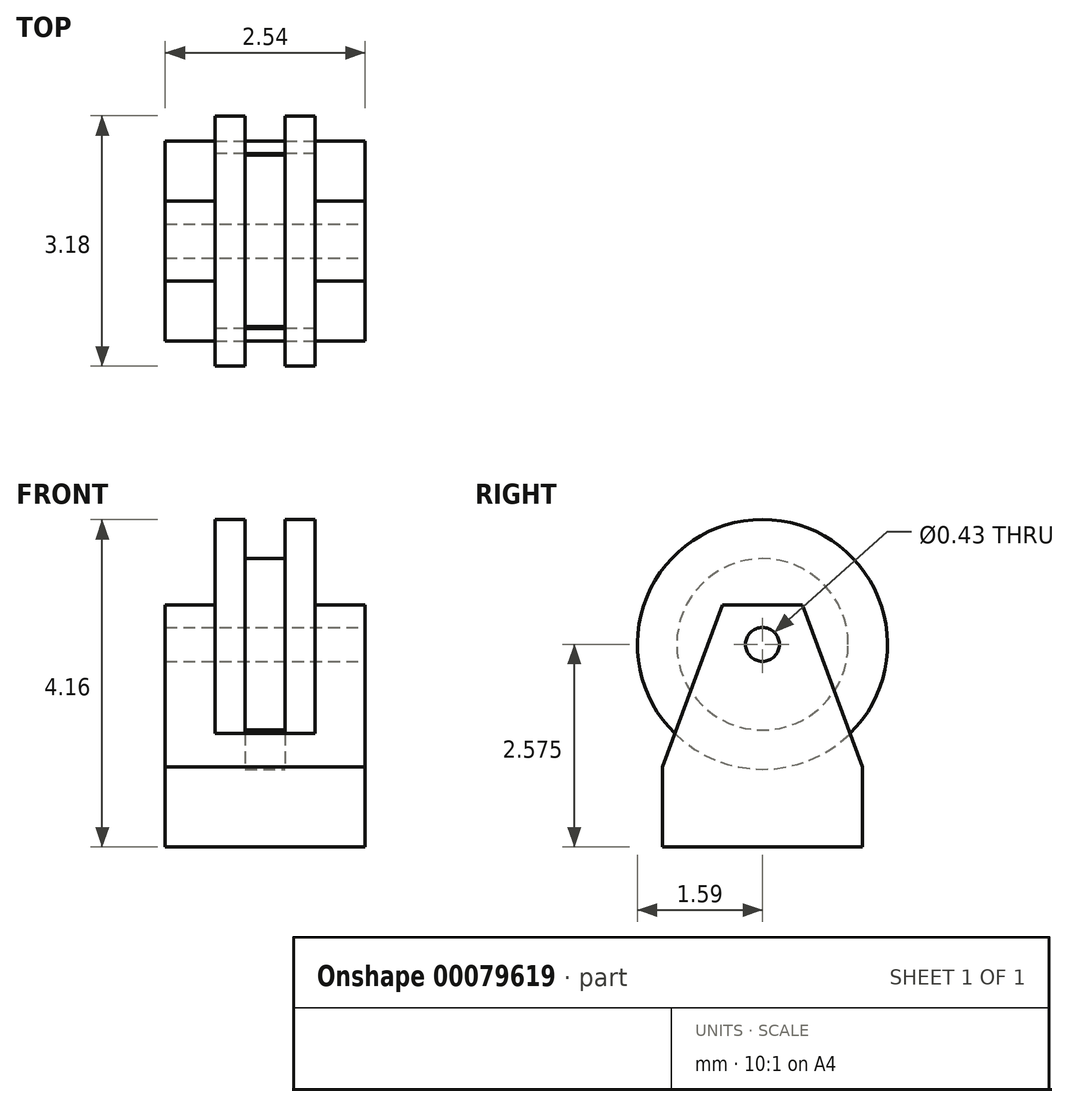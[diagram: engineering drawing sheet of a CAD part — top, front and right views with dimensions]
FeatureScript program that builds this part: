
annotation { "Feature Type Name" : "Feature", "Feature Type Description" : "" }
export const myFeature = defineFeature(function(context is Context, id is Id, definition is map)
    precondition{}
    {
        {
            var Q0;
            Q0=qCreatedBy(makeId("Top.planeOp"),FACE);
            var sketch = newSketch(context, id + "F0", { "sketchPlane" : qUnion([Q0])});
            skLineSegment(sketch, "E0.bottom", {"start": v(-1.27, 1.27) * mm, "end": v(1.27, 1.27) * mm});
            skLineSegment(sketch, "E0.top", {"start": v(-1.27, -1.27) * mm, "end": v(1.27, -1.27) * mm});
            skLineSegment(sketch, "E0.left", {"start": v(-1.27, 1.27) * mm, "end": v(-1.27, -1.27) * mm});
            skLineSegment(sketch, "E0.right", {"start": v(1.27, 1.27) * mm, "end": v(1.27, -1.27) * mm});
            skSolve(sketch);
        }
        {
            var Q0;
            Q0 = qSketchRegion(id + "F0", true);
            extrude(context, id + "F1", {"entities" : qUnion([Q0]), "depth" : 1.02 * mm});
        }
        {
            var Q0;
            Q0=qCreatedBy(makeId("Right.planeOp"),FACE);
            var sketch = newSketch(context, id + "F2", { "sketchPlane" : qUnion([Q0])});
            skCircle(sketch, "E1", {"center": v(0, 2.58) * mm, "radius": 1.59 * mm});
            skSolve(sketch);
        }
        {
            var Q0;
            Q0 = qSketchRegion(id + "F2", true);
            extrude(context, id + "F3", {"entities" : qUnion([Q0]), "operationType" : NewBodyOperationType.ADD, "depth" : 1.27 * mm, "symmetric" : true});
        }
        {
            var Q0;
            Q0=makeQuery(id+"F1.opExtrude","SWEPT_FACE",FACE,{"disambiguationData":[OSD([sQuery(id+"F0.wireOp",EDGE,"E0.right")])]});
            var sketch = newSketch(context, id + "F4", { "sketchPlane" : qUnion([Q0])});
            skLineSegment(sketch, "E2", {"start": v(-1.27, 1.02) * mm, "end": v(-0.5, 3.08) * mm});
            skLineSegment(sketch, "E3", {"start": v(-0.5, 3.08) * mm, "end": v(0.5, 3.08) * mm});
            skLineSegment(sketch, "E4", {"start": v(0.5, 3.08) * mm, "end": v(1.27, 1.02) * mm});
            skLineSegment(sketch, "E5", {"start": v(-1.27, 1.02) * mm, "end": v(1.27, 1.02) * mm});
            skSolve(sketch);
        }
        {
            var Q0;
            Q0 = qSketchRegion(id + "F4", true);
            extrude(context, id + "F5", {"entities" : qUnion([Q0]), "operationType" : NewBodyOperationType.ADD, "oppositeDirection" : true, "depth" : 2.54 * mm});
        }
        {
            var Q0;
            Q0=qCreatedBy(makeId("Right.planeOp"),FACE);
            var sketch = newSketch(context, id + "F6", { "sketchPlane" : qUnion([Q0])});
            skCircle(sketch, "E6", {"center": v(0, 2.58) * mm, "radius": 1.09 * mm});
            skCircle(sketch, "E7", {"center": v(0, 2.58) * mm, "radius": 1.59 * mm});
            skSolve(sketch);
        }
        {
            var Q0;
            Q0 = qSketchRegion(id + "F6", true);
            extrude(context, id + "F7", {"entities" : qUnion([Q0]), "operationType" : NewBodyOperationType.REMOVE, "oppositeDirection" : true, "depth" : 0.5 * mm, "symmetric" : true});
        }
        {
            var Q0;
            Q0=makeQuery(id+"F5.boolean.opBoolean","MERGE",FACE,{"derivedFrom":[makeQuery(id+"F1.opExtrude","SWEPT_FACE",FACE,{"disambiguationData":[OSD([sQuery(id+"F0.wireOp",EDGE,"E0.right")])]}),makeQuery(id+"F5.opExtrude","CAP_FACE",FACE,{"disambiguationData":[OSD([sQuery(id+"F4.wireOp",EDGE,"E2"),sQuery(id+"F4.wireOp",EDGE,"E3"),sQuery(id+"F4.wireOp",EDGE,"E4"),sQuery(id+"F4.wireOp",EDGE,"E5")])],"isStart":true})]});
            var sketch = newSketch(context, id + "F8", { "sketchPlane" : qUnion([Q0])});
            skCircle(sketch, "E8", {"center": v(0, 2.58) * mm, "radius": 0.22 * mm});
            skSolve(sketch);
        }
        {
            var Q0;
            Q0=makeQuery(id+"F8.imprint","IMPRINT",FACE,{"disambiguationData":[TD([[makeQuery(id+"F8.imprint","IMPRINT",EDGE,{"derivedFrom":sQuery(id+"F8.wireOp",EDGE,"E8")}),1.0]])]});
            extrude(context, id + "F9", {"entities" : qUnion([Q0]), "operationType" : NewBodyOperationType.REMOVE, "oppositeDirection" : true, "depth" : 25.4 * mm});
        }
    });
